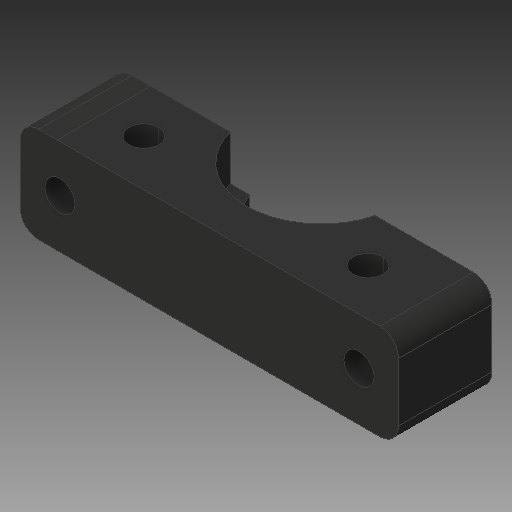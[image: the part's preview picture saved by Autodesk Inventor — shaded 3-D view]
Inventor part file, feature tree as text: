
AUTODESK INVENTOR PART (.ipt)
format: ipt  version: 2018 (Build 220112000, 112)  size: 193,536 bytes
history: native  units: mm
features: sketch x9, other x3
ambient origin geometry x8: Origin, YZ Plane, XZ Plane, XY Plane, X Axis, Y Axis, Z Axis, Center Point
bodies: Solid1 (feature_tree)
feature tree (12):
  other  "Hotend Clamp P2.ipt"
  other  "Solid1::Hotend Clamp P2.ipt"
  other  "TaggingFeature1"
  sketch  "Sketch1"  dims[d0=10.0mm]
  sketch  "Sketch2"
  sketch  "Sketch3"
  sketch  "Sketch4"
  sketch  "Sketch5"
  sketch  "Sketch6"
  sketch  "Sketch7"
  sketch  "Sketch8"
  sketch  "Sketch9"
